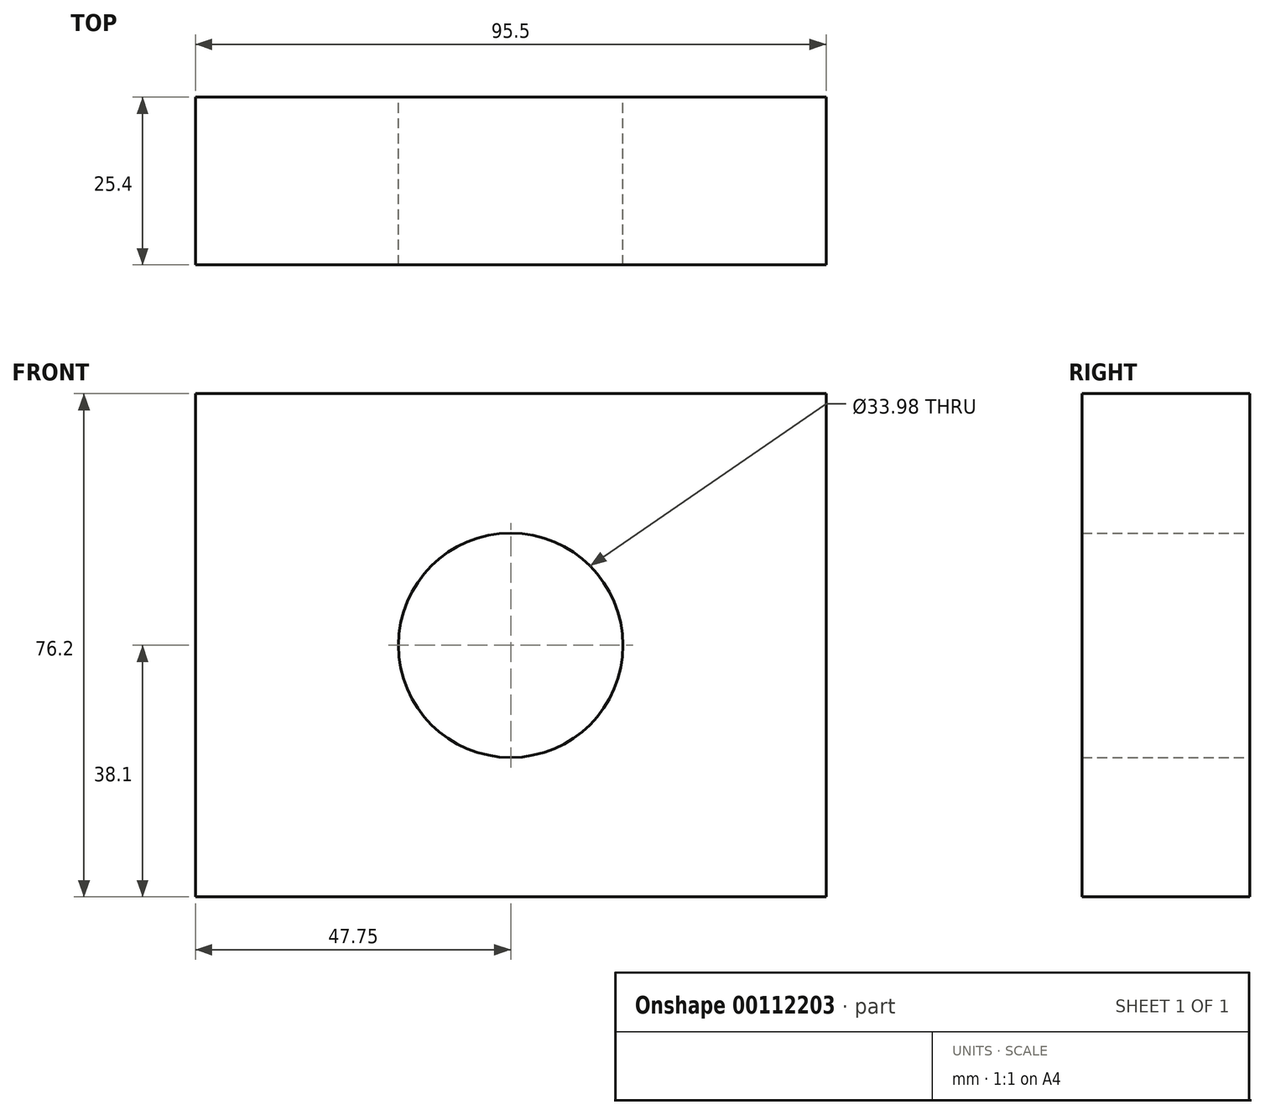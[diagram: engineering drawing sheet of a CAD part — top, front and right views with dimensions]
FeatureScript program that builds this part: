
annotation { "Feature Type Name" : "Feature", "Feature Type Description" : "" }
export const myFeature = defineFeature(function(context is Context, id is Id, definition is map)
    precondition{}
    {
        {
            var Q0;
            Q0=qCreatedBy(makeId("Front.planeOp"),FACE);
            var sketch = newSketch(context, id + "F0", { "sketchPlane" : qUnion([Q0])});
            skLineSegment(sketch, "E0.bottom", {"start": v(-47.75, 38.1) * mm, "end": v(47.75, 38.1) * mm});
            skLineSegment(sketch, "E0.top", {"start": v(-47.75, -38.1) * mm, "end": v(47.75, -38.1) * mm});
            skLineSegment(sketch, "E0.left", {"start": v(-47.75, 38.1) * mm, "end": v(-47.75, -38.1) * mm});
            skLineSegment(sketch, "E0.right", {"start": v(47.75, 38.1) * mm, "end": v(47.75, -38.1) * mm});
            skCircle(sketch, "E1", {"center": v(0, 0) * mm, "radius": 16.99 * mm});
            skSolve(sketch);
        }
        {
            var Q0;
            Q0 = qSketchRegion(id + "F0", true);
            extrude(context, id + "F1", {"entities" : qUnion([Q0]), "depth" : 25.4 * mm});
        }
    });
